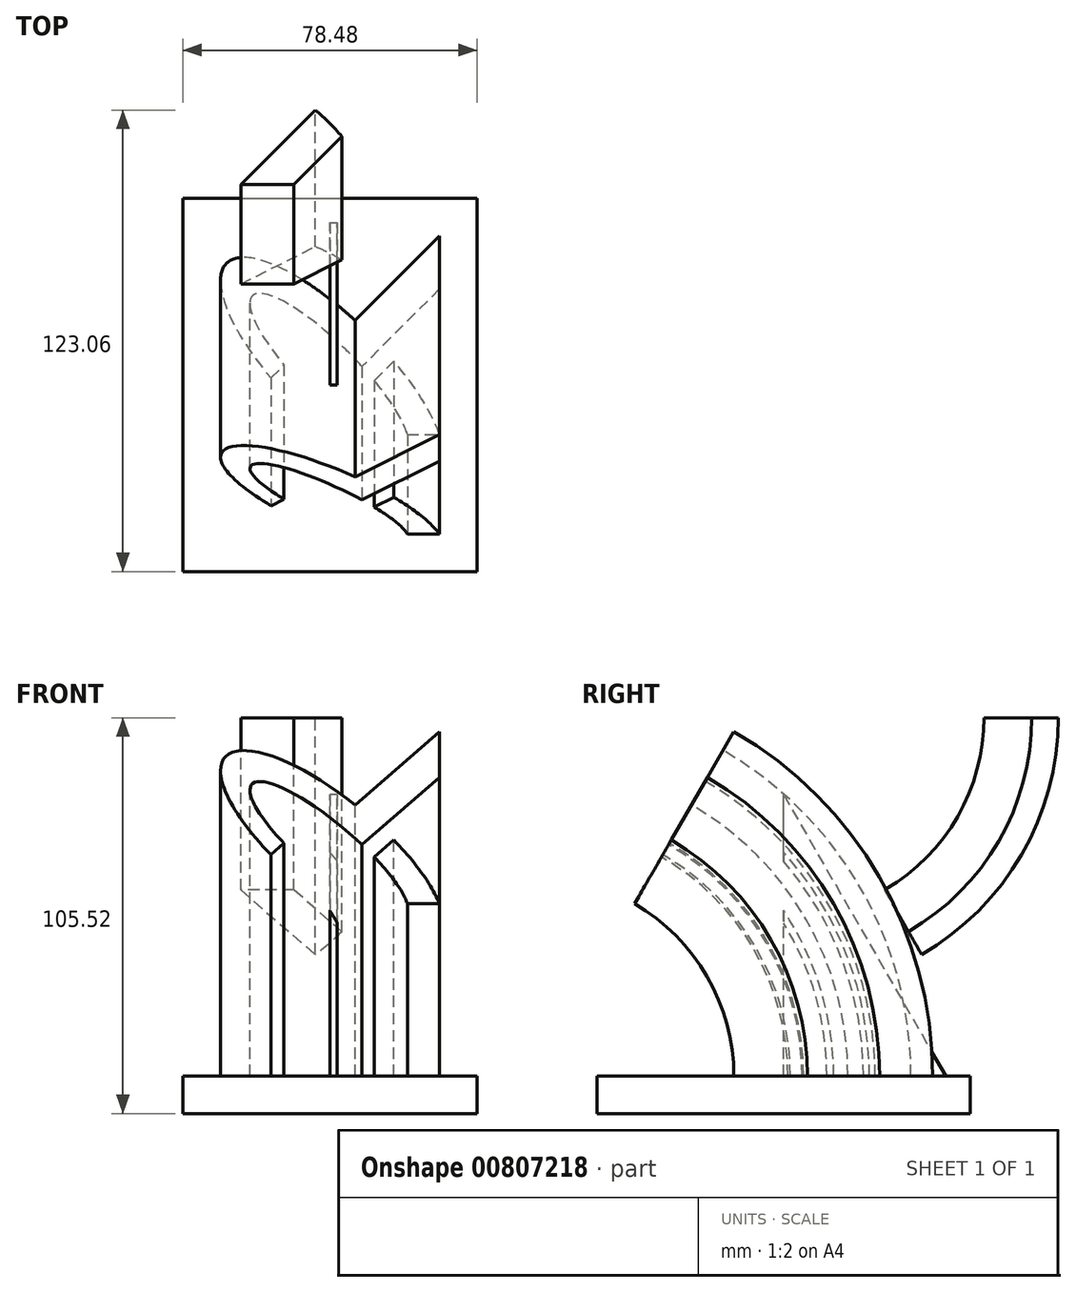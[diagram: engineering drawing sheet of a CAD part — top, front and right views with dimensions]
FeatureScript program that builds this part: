
annotation { "Feature Type Name" : "Feature", "Feature Type Description" : "" }
export const myFeature = defineFeature(function(context is Context, id is Id, definition is map)
    precondition{}
    {
        {
            var Q0;
            Q0=qCreatedBy(makeId("Front.planeOp"),FACE);
            var sketch = newSketch(context, id + "F0", { "sketchPlane" : qUnion([Q0])});
            skLineSegment(sketch, "E0", {"start": v(-24.75, -17.68) * mm, "end": v(-4.71, 2.36) * mm});
            skLineSegment(sketch, "E1", {"start": v(28.28, 35.36) * mm, "end": v(28.28, 21.21) * mm});
            skLineSegment(sketch, "E2", {"start": v(28.28, 21.21) * mm, "end": v(7.58, 0.5) * mm});
            skLineSegment(sketch, "E3", {"start": v(-10.6, -17.68) * mm, "end": v(-24.75, -17.68) * mm});
            skLineSegment(sketch, "E4", {"start": v(-17.68, -17.68) * mm, "end": v(28.28, 28.28) * mm, "construction": true});
            skPoint(sketch, "E5", {"position": v(-0.32, -0.32) * mm});
            skPoint(sketch, "E6", {"position": v(-1.18, -1.18) * mm});
            skLineSegment(sketch, "E7", {"start": v(-33.94, 22.63) * mm, "end": v(-21.26, 35.31) * mm, "construction": true});
            skLineSegment(sketch, "E8", {"start": v(-0.32, -0.32) * mm, "end": v(-28.6, 27.97) * mm, "construction": true});
            skLineSegment(sketch, "E9", {"start": v(1.14, 17.5) * mm, "end": v(20.2, -1.55) * mm, "construction": true});
            skEllipticalArc(sketch, "E10", {"construction": true});
            skPoint(sketch, "E11.orphan", {"position": v(9.33, 9.33) * mm});
            skLineSegment(sketch, "E12", {"start": v(-32.75, 8.26) * mm, "end": v(-10.1, 30.9) * mm, "construction": true});
            skLineSegment(sketch, "E13", {"start": v(-1.89, 10.14) * mm, "end": v(11.83, -3.58) * mm, "construction": true});
            skLineSegment(sketch, "E14", {"start": v(-1.18, -1.18) * mm, "end": v(-21.68, 19.33) * mm, "construction": true});
            skPoint(sketch, "E15", {"position": v(4.12, 4.12) * mm});
            skEllipticalArc(sketch, "E16", {"construction": true});
            skLineSegment(sketch, "E17", {"start": v(-10.6, -17.68) * mm, "end": v(45.02, -17.68) * mm, "construction": true});
            skLineSegment(sketch, "E18", {"start": v(28.28, 21.21) * mm, "end": v(28.28, -17.68) * mm, "construction": true});
            skLineSegment(sketch, "E19", {"start": v(-16.73, -2.59) * mm, "end": v(-13.23, 0.91) * mm});
            skEllipticalArc(sketch, "E20.trimOffspring", {});
            skEllipticalArc(sketch, "E21.trimOffspring", {});
            skLineSegment(sketch, "E22", {"start": v(19.7, -17.68) * mm, "end": v(28.28, -17.68) * mm});
            skLineSegment(sketch, "E23", {"start": v(10.87, -3.27) * mm, "end": v(16.1, 1.95) * mm});
            skEllipticalArc(sketch, "E24.trimOffspring", {});
            skEllipticalArc(sketch, "E25.trimOffspring", {});
            skPoint(sketch, "E26", {"position": v(-17.16, -2.07) * mm});
            skLineSegment(sketch, "E27", {"start": v(-30.2, 39.56) * mm, "end": v(-30.2, -18.08) * mm, "construction": true});
            skLineSegment(sketch, "E28", {"start": v(-69.2, -70.71) * mm, "end": v(103.78, -70.71) * mm, "construction": true});
            skLineSegment(sketch, "E29", {"start": v(37.18, -17.68) * mm, "end": v(37.18, -70.71) * mm, "construction": true});
            skLineSegment(sketch, "E30", {"start": v(37.18, -17.68) * mm, "end": v(37.18, 35.36) * mm, "construction": true});
            skArc(sketch, "E31", {"start": v(2.18, -4.89) * mm, "mid": v(-1.18, -1.18) * mm, "end": v(-4.9, 2.18) * mm});
            skLineSegment(sketch, "E32.trimOffspring", {"start": v(0.5, 7.58) * mm, "end": v(28.28, 35.36) * mm});
            skLineSegment(sketch, "E33.trimOffspring", {"start": v(2.18, -4.89) * mm, "end": v(-10.6, -17.68) * mm});
            const initialGuessF0  = {"E10": [-0.00031912991471063317, -0.0003191299147105802, -0.7071067811865474, 0.7071067811865477, 0.04, 0.013639532062820101, 1.696124157962962, 1.8619759006274477], "E16": [-0.0011785113019775794, -0.0011785113019775768, -0.7071067811865482, 0.7071067811865468, 0.029, 0.0075, 1.744075963212437, 2.210740282484098], "E20.trimOffspring": [-0.0011785113019775794, -0.0011785113019775768, -0.7071067811865482, 0.7071067811865468, 0.029, 0.0075, 3.566293720366283, 4.360333881075686], "E21.trimOffspring": [-0.00031912991471063317, -0.0003191299147105802, -0.7071067811865474, 0.7071067811865477, 0.04, 0.013639532062820101, 3.763961142144815, 4.459708725242612], "E24.trimOffspring": [-0.0011785113019775794, -0.0011785113019775768, -0.7071067811865482, 0.7071067811865468, 0.029, 0.0075, 4.539109343967149, 1.2187412274858924], "E25.trimOffspring": [-0.00031912991471063317, -0.0003191299147105802, -0.7071067811865474, 0.7071067811865477, 0.04, 0.013639532062820101, 4.587061149216624, 1.3181160716528182]};
            skSetInitialGuess(sketch, initialGuessF0);
            skSolve(sketch);
        }
        {
            var Q0;
            Q0 = qSketchRegion(id + "F0", true);
            var Q1;
            Q1=sQuery(id+"F0.wireOp",EDGE,"E28");
            revolve(context, id + "F1", {"surfaceOperationType" : NewSurfaceOperationType.NEW, "entities" : qUnion([Q0]), "axis" : qUnion([Q1]), "revolveType" : RevolveType.ONE_DIRECTION, "oppositeDirection" : true, "angle" : 60 * degree});
        }
        {
            var Q0;
            Q0=makeQuery(id+"F1.opRevolve","SWEPT_BODY",BODY,{"disambiguationData":[OSD([sQuery(id+"F0.wireOp",EDGE,"E0"),sQuery(id+"F0.wireOp",EDGE,"E3"),sQuery(id+"F0.wireOp",EDGE,"E31"),sQuery(id+"F0.wireOp",EDGE,"E33.trimOffspring")])]});
            var Q1;
            Q1=makeQuery(id+"F1.opRevolve","SWEPT_BODY",BODY,{"disambiguationData":[OSD([sQuery(id+"F0.wireOp",EDGE,"E1"),sQuery(id+"F0.wireOp",EDGE,"E2"),sQuery(id+"F0.wireOp",EDGE,"E19"),sQuery(id+"F0.wireOp",EDGE,"E24.trimOffspring"),sQuery(id+"F0.wireOp",EDGE,"E25.trimOffspring"),sQuery(id+"F0.wireOp",EDGE,"E32.trimOffspring")])]});
            var Q2;
            Q2=makeQuery(id+"F1.opRevolve","SWEPT_BODY",BODY,{"disambiguationData":[OSD([sQuery(id+"F0.wireOp",EDGE,"E20.trimOffspring"),sQuery(id+"F0.wireOp",EDGE,"E21.trimOffspring"),sQuery(id+"F0.wireOp",EDGE,"E22"),sQuery(id+"F0.wireOp",EDGE,"E23")])]});
            var Q3;
            Q3=sQuery(id+"F0.wireOp",EDGE,"E28");
            transform(context, id + "F2", {"entities" : qUnion([Q0, Q1, Q2]), "transformType" : TransformType.ROTATION, "transformAxis" : qUnion([Q3]), "angle" : 30 * degree, "oppositeDirection" : true, "makeCopy" : false});
        }
        {
            var Q0;
            Q0=makeQuery(id+"F1.opRevolve","CAP_FACE",FACE,{"disambiguationData":[OSD([sQuery(id+"F0.wireOp",EDGE,"E1"),sQuery(id+"F0.wireOp",EDGE,"E2"),sQuery(id+"F0.wireOp",EDGE,"E19"),sQuery(id+"F0.wireOp",EDGE,"E24.trimOffspring"),sQuery(id+"F0.wireOp",EDGE,"E25.trimOffspring"),sQuery(id+"F0.wireOp",EDGE,"E32.trimOffspring")])],"isStart":false});
            var sketch = newSketch(context, id + "F3", { "sketchPlane" : qUnion([Q0])});
            skLineSegment(sketch, "E34.bottom", {"start": v(-40.2, -16.52) * mm, "end": v(38.28, -16.52) * mm});
            skLineSegment(sketch, "E34.top", {"start": v(-40.2, -116.07) * mm, "end": v(38.28, -116.07) * mm});
            skLineSegment(sketch, "E34.left", {"start": v(-40.2, -16.52) * mm, "end": v(-40.2, -116.07) * mm});
            skLineSegment(sketch, "E34.right", {"start": v(38.28, -16.52) * mm, "end": v(38.28, -116.07) * mm});
            skLineSegment(sketch, "E35", {"start": v(-30.2, 6.86) * mm, "end": v(-30.2, -4.56) * mm, "construction": true});
            skLineSegment(sketch, "E36", {"start": v(-21.32, -106.07) * mm, "end": v(26.08, -106.07) * mm, "construction": true});
            skSolve(sketch);
        }
        {
            var Q0;
            Q0 = qSketchRegion(id + "F3", true);
            extrude(context, id + "F4", {"entities" : qUnion([Q0]), "depth" : 10 * mm, "offsetDistance" : 25 * mm});
        }
        {
            var Q0;
            Q0=makeQuery(id+"F1.opRevolve","SWEPT_BODY",BODY,{"disambiguationData":[OSD([sQuery(id+"F0.wireOp",EDGE,"E0"),sQuery(id+"F0.wireOp",EDGE,"E3"),sQuery(id+"F0.wireOp",EDGE,"E31"),sQuery(id+"F0.wireOp",EDGE,"E33.trimOffspring")])]});
            var Q1;
            Q1=makeQuery(id+"F4.opExtrude","CAP_EDGE",EDGE,{"disambiguationData":[OSD([sQuery(id+"F3.wireOp",EDGE,"E34.top")])],"isStart":false});
            transform(context, id + "F5", {"entities" : qUnion([Q0]), "transformType" : TransformType.ROTATION, "transformAxis" : qUnion([Q1]), "angle" : 60 * degree, "oppositeDirection" : true, "makeCopy" : false});
        }
        {
            var Q0;
            Q0=qCreatedBy(makeId("Right.planeOp"),FACE);
            var sketch = newSketch(context, id + "F6", { "sketchPlane" : qUnion([Q0])});
            skLineSegment(sketch, "E37", {"start": v(66.3, 4.3) * mm, "end": v(115.37, -80.71) * mm});
            skLineSegment(sketch, "E38", {"start": v(115.37, -80.71) * mm, "end": v(66.3, -80.71) * mm});
            skLineSegment(sketch, "E39", {"start": v(66.3, -80.71) * mm, "end": v(66.3, 4.3) * mm});
            skSolve(sketch);
        }
        {
            var Q0;
            {var subQ0=sQuery(id+"F6.wireOp",EDGE,"E38");Q0=makeQuery(id+"F6.imprint","IMPRINT",FACE,{"disambiguationData":[TD([[makeQuery(id+"F6.imprint","IMPRINT",EDGE,{"derivedFrom":subQ0}),-1.0]])]});}
            extrude(context, id + "F7", {"entities" : qUnion([Q0]), "operationType" : NewBodyOperationType.ADD, "endBound" : BoundingType.SYMMETRIC, "depth" : 2 * mm, "offsetDistance" : 25 * mm});
        }
    });
